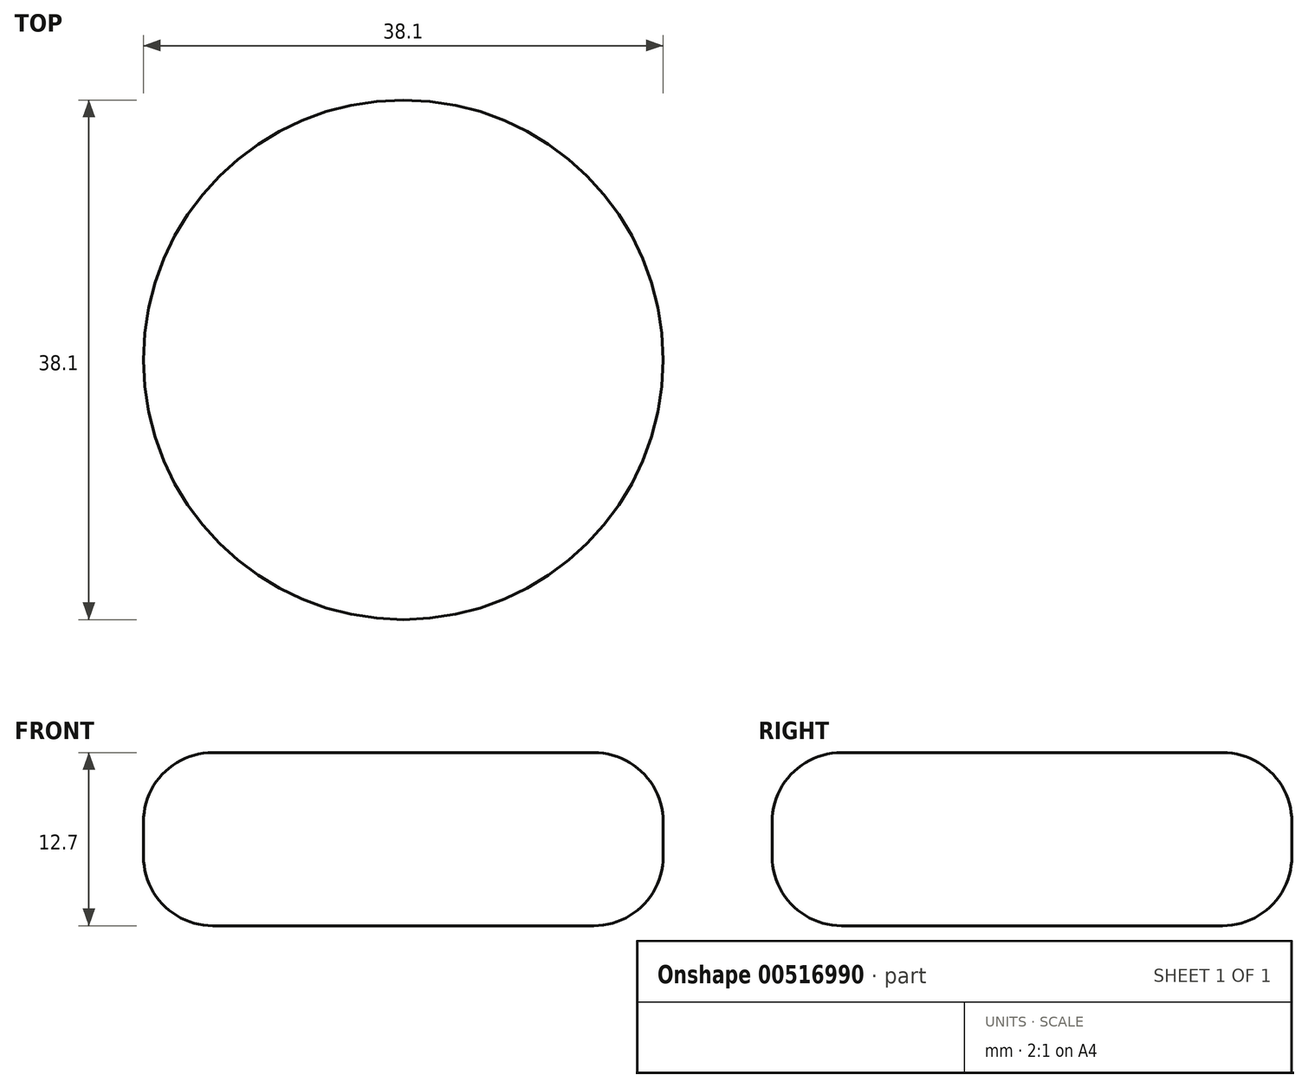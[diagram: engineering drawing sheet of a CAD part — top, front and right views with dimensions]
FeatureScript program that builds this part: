
annotation { "Feature Type Name" : "Feature", "Feature Type Description" : "" }
export const myFeature = defineFeature(function(context is Context, id is Id, definition is map)
    precondition{}
    {
        {
            var Q0;
            Q0=qCreatedBy(makeId("Top.planeOp"),FACE);
            var sketch = newSketch(context, id + "F0", { "sketchPlane" : qUnion([Q0])});
            skCircle(sketch, "E0", {"center": v(0, 0) * mm, "radius": 19.05 * mm});
            skSolve(sketch);
        }
        {
            var Q0;
            Q0 = qSketchRegion(id + "F0", true);
            extrude(context, id + "F1", {"entities" : qUnion([Q0]), "depth" : 12.7 * mm, "offsetDistance" : 25.4 * mm});
        }
        {
            var Q0;
            Q0=makeQuery(id+"F1.opExtrude","SWEPT_FACE",FACE,{"disambiguationData":[OSD([sQuery(id+"F0.wireOp",EDGE,"E0")])]});
            fillet(context, id + "F2", {"entities" : qUnion([Q0]), "radius" : 5.08 * mm, "tangentPropagation" : true, "allowEdgeOverflow" : false});
        }
    });
